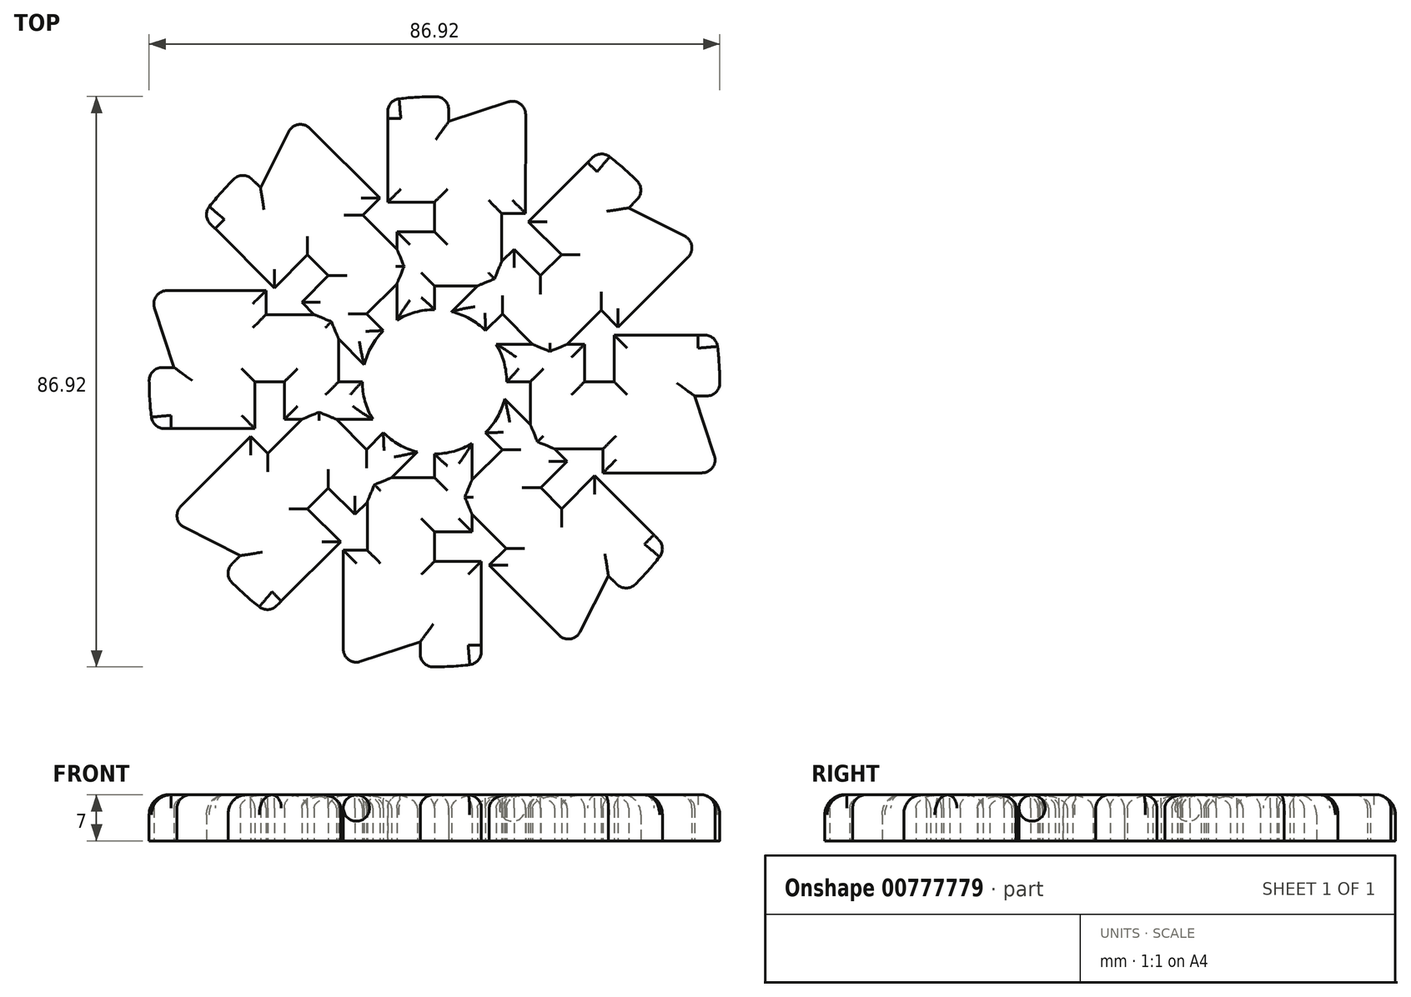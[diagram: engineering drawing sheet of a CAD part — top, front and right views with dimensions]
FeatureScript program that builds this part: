
annotation { "Feature Type Name" : "Feature", "Feature Type Description" : "" }
export const myFeature = defineFeature(function(context is Context, id is Id, definition is map)
    precondition{}
    {
        {
            var Q0;
            Q0=qCreatedBy(makeId("Top.planeOp"),FACE);
            var sketch = newSketch(context, id + "F0", { "sketchPlane" : qUnion([Q0])});
            skCircle(sketch, "E0", {"center": v(0, 0) * mm, "radius": 35 * mm});
            skCircle(sketch, "E1", {"center": v(0, 0) * mm, "radius": 11 * mm});
            skSolve(sketch);
        }
        {
            var Q0;
            Q0=qCreatedBy(makeId("Top.planeOp"),FACE);
            var sketch = newSketch(context, id + "F1", { "sketchPlane" : qUnion([Q0])});
            skLineSegment(sketch, "E2.top", {"start": v(0, 22.87) * mm, "end": v(-5.72, 22.87) * mm});
            skLineSegment(sketch, "E2.right", {"start": v(-5.72, 9.4) * mm, "end": v(-5.72, 22.87) * mm});
            skLineSegment(sketch, "E3.top", {"start": v(0, 14.6) * mm, "end": v(10.24, 14.6) * mm});
            skLineSegment(sketch, "E3.right", {"start": v(10.24, 25.67) * mm, "end": v(10.24, 14.6) * mm});
            skLineSegment(sketch, "E4.bottom", {"start": v(2.18, 39.65) * mm, "end": v(13.89, 43.5) * mm});
            skLineSegment(sketch, "E4.left", {"start": v(0, 27.37) * mm, "end": v(0, 22.87) * mm});
            skLineSegment(sketch, "E4.right", {"start": v(13.89, 43.5) * mm, "end": v(13.88, 25.67) * mm});
            skLineSegment(sketch, "E5.top", {"start": v(-7.13, 27.37) * mm, "end": v(0, 27.37) * mm});
            skPoint(sketch, "E6.orphan", {"position": v(0, 38.94) * mm});
            skLineSegment(sketch, "E7.trimOffspring", {"start": v(10.24, 25.67) * mm, "end": v(13.88, 25.67) * mm});
            skArc(sketch, "E8", {"start": v(0, 11) * mm, "mid": v(-2.97, 10.6) * mm, "end": v(-5.72, 9.4) * mm});
            skLineSegment(sketch, "E9", {"start": v(0, 14.6) * mm, "end": v(0, 11) * mm});
            skLineSegment(sketch, "E10", {"start": v(-7.13, 27.37) * mm, "end": v(-7.13, 42.87) * mm});
            skLineSegment(sketch, "E11", {"start": v(2.18, 39.65) * mm, "end": v(2.18, 43.41) * mm});
            skArc(sketch, "E12", {"start": v(2.18, 43.41) * mm, "mid": v(-2.5, 43.38) * mm, "end": v(-7.13, 42.87) * mm});
            skLineSegment(sketch, "E13.1.0", {"start": v(-16.17, 16.16) * mm, "end": v(-20.21, 12.13) * mm});
            skLineSegment(sketch, "E13.1.1", {"start": v(-10.33, 10.33) * mm, "end": v(-7.78, 7.78) * mm});
            skLineSegment(sketch, "E13.1.2", {"start": v(-20.94, 40.59) * mm, "end": v(-8.34, 27.97) * mm});
            skLineSegment(sketch, "E13.1.3", {"start": v(-10.33, 10.33) * mm, "end": v(-3.09, 17.57) * mm});
            skPoint(sketch, "E13.1.4", {"position": v(-27.53, 27.53) * mm});
            skLineSegment(sketch, "E13.1.5", {"start": v(-19.36, 19.35) * mm, "end": v(-16.17, 16.16) * mm});
            skLineSegment(sketch, "E13.1.6", {"start": v(-10.69, 2.6) * mm, "end": v(-20.21, 12.13) * mm});
            skLineSegment(sketch, "E13.1.7", {"start": v(-24.4, 14.3) * mm, "end": v(-35.36, 25.27) * mm});
            skLineSegment(sketch, "E13.1.8", {"start": v(-26.5, 29.58) * mm, "end": v(-20.94, 40.59) * mm});
            skLineSegment(sketch, "E13.1.9", {"start": v(-26.5, 29.58) * mm, "end": v(-22.7, 25.77) * mm});
            skArc(sketch, "E13.1.10", {"start": v(-29.16, 32.24) * mm, "mid": v(-32.44, 28.91) * mm, "end": v(-35.36, 25.27) * mm});
            skLineSegment(sketch, "E13.1.11", {"start": v(-10.91, 25.4) * mm, "end": v(-3.09, 17.57) * mm});
            skLineSegment(sketch, "E13.1.12", {"start": v(-24.4, 14.3) * mm, "end": v(-19.36, 19.35) * mm});
            skArc(sketch, "E13.1.13", {"start": v(-7.78, 7.78) * mm, "mid": v(-9.59, 5.39) * mm, "end": v(-10.69, 2.6) * mm});
            skLineSegment(sketch, "E13.1.14", {"start": v(-10.91, 25.4) * mm, "end": v(-8.34, 27.97) * mm});
            skLineSegment(sketch, "E13.1.15", {"start": v(-22.7, 25.77) * mm, "end": v(-29.16, 32.24) * mm});
            skLineSegment(sketch, "E13.2.0", {"start": v(-22.87, 0) * mm, "end": v(-22.87, -5.72) * mm});
            skLineSegment(sketch, "E13.2.1", {"start": v(-14.6, 0) * mm, "end": v(-11, 0) * mm});
            skLineSegment(sketch, "E13.2.2", {"start": v(-43.5, 13.89) * mm, "end": v(-25.67, 13.88) * mm});
            skLineSegment(sketch, "E13.2.3", {"start": v(-14.6, 0) * mm, "end": v(-14.6, 10.24) * mm});
            skPoint(sketch, "E13.2.4", {"position": v(-38.94, 0) * mm});
            skLineSegment(sketch, "E13.2.5", {"start": v(-27.37, 0) * mm, "end": v(-22.87, 0) * mm});
            skLineSegment(sketch, "E13.2.6", {"start": v(-9.4, -5.72) * mm, "end": v(-22.87, -5.72) * mm});
            skLineSegment(sketch, "E13.2.7", {"start": v(-27.37, -7.13) * mm, "end": v(-42.87, -7.13) * mm});
            skLineSegment(sketch, "E13.2.8", {"start": v(-39.65, 2.18) * mm, "end": v(-43.5, 13.89) * mm});
            skLineSegment(sketch, "E13.2.9", {"start": v(-39.65, 2.18) * mm, "end": v(-34.27, 2.18) * mm});
            skArc(sketch, "E13.2.10", {"start": v(-43.41, 2.18) * mm, "mid": v(-43.38, -2.5) * mm, "end": v(-42.87, -7.13) * mm});
            skLineSegment(sketch, "E13.2.11", {"start": v(-25.67, 10.24) * mm, "end": v(-14.6, 10.24) * mm});
            skLineSegment(sketch, "E13.2.12", {"start": v(-27.37, -7.13) * mm, "end": v(-27.37, 0) * mm});
            skArc(sketch, "E13.2.13", {"start": v(-11, 0) * mm, "mid": v(-10.6, -2.97) * mm, "end": v(-9.4, -5.72) * mm});
            skLineSegment(sketch, "E13.2.14", {"start": v(-25.67, 10.24) * mm, "end": v(-25.67, 13.88) * mm});
            skLineSegment(sketch, "E13.2.15", {"start": v(-34.27, 2.18) * mm, "end": v(-43.41, 2.18) * mm});
            skLineSegment(sketch, "E13.3.0", {"start": v(-16.16, -16.17) * mm, "end": v(-12.13, -20.21) * mm});
            skLineSegment(sketch, "E13.3.1", {"start": v(-10.33, -10.33) * mm, "end": v(-7.78, -7.78) * mm});
            skLineSegment(sketch, "E13.3.2", {"start": v(-40.59, -20.94) * mm, "end": v(-27.97, -8.34) * mm});
            skLineSegment(sketch, "E13.3.3", {"start": v(-10.33, -10.33) * mm, "end": v(-17.57, -3.09) * mm});
            skPoint(sketch, "E13.3.4", {"position": v(-27.53, -27.53) * mm});
            skLineSegment(sketch, "E13.3.5", {"start": v(-19.35, -19.36) * mm, "end": v(-16.16, -16.17) * mm});
            skLineSegment(sketch, "E13.3.6", {"start": v(-2.6, -10.69) * mm, "end": v(-12.13, -20.21) * mm});
            skLineSegment(sketch, "E13.3.7", {"start": v(-14.3, -24.4) * mm, "end": v(-25.27, -35.36) * mm});
            skLineSegment(sketch, "E13.3.8", {"start": v(-29.58, -26.5) * mm, "end": v(-40.59, -20.94) * mm});
            skLineSegment(sketch, "E13.3.9", {"start": v(-29.58, -26.5) * mm, "end": v(-25.77, -22.7) * mm});
            skArc(sketch, "E13.3.10", {"start": v(-32.24, -29.16) * mm, "mid": v(-28.91, -32.44) * mm, "end": v(-25.27, -35.36) * mm});
            skLineSegment(sketch, "E13.3.11", {"start": v(-25.4, -10.91) * mm, "end": v(-17.57, -3.09) * mm});
            skLineSegment(sketch, "E13.3.12", {"start": v(-14.3, -24.4) * mm, "end": v(-19.35, -19.36) * mm});
            skArc(sketch, "E13.3.13", {"start": v(-7.78, -7.78) * mm, "mid": v(-5.39, -9.59) * mm, "end": v(-2.6, -10.69) * mm});
            skLineSegment(sketch, "E13.3.14", {"start": v(-25.4, -10.91) * mm, "end": v(-27.97, -8.34) * mm});
            skLineSegment(sketch, "E13.3.15", {"start": v(-25.77, -22.7) * mm, "end": v(-32.24, -29.16) * mm});
            skLineSegment(sketch, "E13.4.0", {"start": v(0, -22.87) * mm, "end": v(5.72, -22.87) * mm});
            skLineSegment(sketch, "E13.4.1", {"start": v(0, -14.6) * mm, "end": v(0, -11) * mm});
            skLineSegment(sketch, "E13.4.2", {"start": v(-13.89, -43.5) * mm, "end": v(-13.88, -25.67) * mm});
            skLineSegment(sketch, "E13.4.3", {"start": v(0, -14.6) * mm, "end": v(-10.24, -14.6) * mm});
            skPoint(sketch, "E13.4.4", {"position": v(0, -38.94) * mm});
            skLineSegment(sketch, "E13.4.5", {"start": v(0, -27.37) * mm, "end": v(0, -22.87) * mm});
            skLineSegment(sketch, "E13.4.6", {"start": v(5.72, -9.4) * mm, "end": v(5.72, -22.87) * mm});
            skLineSegment(sketch, "E13.4.7", {"start": v(7.13, -27.37) * mm, "end": v(7.13, -42.87) * mm});
            skLineSegment(sketch, "E13.4.8", {"start": v(-2.18, -39.65) * mm, "end": v(-13.89, -43.5) * mm});
            skLineSegment(sketch, "E13.4.9", {"start": v(-2.18, -39.65) * mm, "end": v(-2.18, -34.27) * mm});
            skArc(sketch, "E13.4.10", {"start": v(-2.18, -43.41) * mm, "mid": v(2.5, -43.38) * mm, "end": v(7.13, -42.87) * mm});
            skLineSegment(sketch, "E13.4.11", {"start": v(-10.24, -25.67) * mm, "end": v(-10.24, -14.6) * mm});
            skLineSegment(sketch, "E13.4.12", {"start": v(7.13, -27.37) * mm, "end": v(0, -27.37) * mm});
            skArc(sketch, "E13.4.13", {"start": v(0, -11) * mm, "mid": v(2.97, -10.6) * mm, "end": v(5.72, -9.4) * mm});
            skLineSegment(sketch, "E13.4.14", {"start": v(-10.24, -25.67) * mm, "end": v(-13.88, -25.67) * mm});
            skLineSegment(sketch, "E13.4.15", {"start": v(-2.18, -34.27) * mm, "end": v(-2.18, -43.41) * mm});
            skLineSegment(sketch, "E13.5.0", {"start": v(16.17, -16.16) * mm, "end": v(20.21, -12.13) * mm});
            skLineSegment(sketch, "E13.5.1", {"start": v(10.33, -10.33) * mm, "end": v(7.78, -7.78) * mm});
            skLineSegment(sketch, "E13.5.2", {"start": v(20.94, -40.59) * mm, "end": v(8.34, -27.97) * mm});
            skLineSegment(sketch, "E13.5.3", {"start": v(10.33, -10.33) * mm, "end": v(3.09, -17.57) * mm});
            skPoint(sketch, "E13.5.4", {"position": v(27.53, -27.53) * mm});
            skLineSegment(sketch, "E13.5.5", {"start": v(19.36, -19.35) * mm, "end": v(16.17, -16.16) * mm});
            skLineSegment(sketch, "E13.5.6", {"start": v(10.69, -2.6) * mm, "end": v(20.21, -12.13) * mm});
            skLineSegment(sketch, "E13.5.7", {"start": v(24.4, -14.3) * mm, "end": v(35.36, -25.27) * mm});
            skLineSegment(sketch, "E13.5.8", {"start": v(26.5, -29.58) * mm, "end": v(20.94, -40.59) * mm});
            skLineSegment(sketch, "E13.5.9", {"start": v(26.5, -29.58) * mm, "end": v(22.7, -25.77) * mm});
            skArc(sketch, "E13.5.10", {"start": v(29.16, -32.24) * mm, "mid": v(32.44, -28.91) * mm, "end": v(35.36, -25.27) * mm});
            skLineSegment(sketch, "E13.5.11", {"start": v(10.91, -25.4) * mm, "end": v(3.09, -17.57) * mm});
            skLineSegment(sketch, "E13.5.12", {"start": v(24.4, -14.3) * mm, "end": v(19.36, -19.35) * mm});
            skArc(sketch, "E13.5.13", {"start": v(7.78, -7.78) * mm, "mid": v(9.59, -5.39) * mm, "end": v(10.69, -2.6) * mm});
            skLineSegment(sketch, "E13.5.14", {"start": v(10.91, -25.4) * mm, "end": v(8.34, -27.97) * mm});
            skLineSegment(sketch, "E13.5.15", {"start": v(22.7, -25.77) * mm, "end": v(29.16, -32.24) * mm});
            skLineSegment(sketch, "E13.6.0", {"start": v(22.87, 0) * mm, "end": v(22.87, 5.72) * mm});
            skLineSegment(sketch, "E13.6.1", {"start": v(14.6, 0) * mm, "end": v(11, 0) * mm});
            skLineSegment(sketch, "E13.6.2", {"start": v(43.5, -13.89) * mm, "end": v(25.67, -13.88) * mm});
            skLineSegment(sketch, "E13.6.3", {"start": v(14.6, 0) * mm, "end": v(14.6, -10.24) * mm});
            skPoint(sketch, "E13.6.4", {"position": v(38.94, 0) * mm});
            skLineSegment(sketch, "E13.6.5", {"start": v(27.37, 0) * mm, "end": v(22.87, 0) * mm});
            skLineSegment(sketch, "E13.6.6", {"start": v(9.4, 5.72) * mm, "end": v(22.87, 5.72) * mm});
            skLineSegment(sketch, "E13.6.7", {"start": v(27.37, 7.13) * mm, "end": v(42.87, 7.13) * mm});
            skLineSegment(sketch, "E13.6.8", {"start": v(39.65, -2.18) * mm, "end": v(43.5, -13.89) * mm});
            skLineSegment(sketch, "E13.6.9", {"start": v(39.65, -2.18) * mm, "end": v(34.27, -2.18) * mm});
            skArc(sketch, "E13.6.10", {"start": v(43.41, -2.18) * mm, "mid": v(43.38, 2.5) * mm, "end": v(42.87, 7.13) * mm});
            skLineSegment(sketch, "E13.6.11", {"start": v(25.67, -10.24) * mm, "end": v(14.6, -10.24) * mm});
            skLineSegment(sketch, "E13.6.12", {"start": v(27.37, 7.13) * mm, "end": v(27.37, 0) * mm});
            skArc(sketch, "E13.6.13", {"start": v(11, 0) * mm, "mid": v(10.6, 2.97) * mm, "end": v(9.4, 5.72) * mm});
            skLineSegment(sketch, "E13.6.14", {"start": v(25.67, -10.24) * mm, "end": v(25.67, -13.88) * mm});
            skLineSegment(sketch, "E13.6.15", {"start": v(34.27, -2.18) * mm, "end": v(43.41, -2.18) * mm});
            skLineSegment(sketch, "E13.7.0", {"start": v(16.16, 16.17) * mm, "end": v(12.13, 20.21) * mm});
            skLineSegment(sketch, "E13.7.1", {"start": v(10.33, 10.33) * mm, "end": v(7.78, 7.78) * mm});
            skLineSegment(sketch, "E13.7.2", {"start": v(40.59, 20.94) * mm, "end": v(27.97, 8.34) * mm});
            skLineSegment(sketch, "E13.7.3", {"start": v(10.33, 10.33) * mm, "end": v(17.57, 3.09) * mm});
            skPoint(sketch, "E13.7.4", {"position": v(27.53, 27.53) * mm});
            skLineSegment(sketch, "E13.7.5", {"start": v(19.35, 19.36) * mm, "end": v(16.16, 16.17) * mm});
            skLineSegment(sketch, "E13.7.6", {"start": v(2.6, 10.69) * mm, "end": v(12.13, 20.21) * mm});
            skLineSegment(sketch, "E13.7.7", {"start": v(14.3, 24.4) * mm, "end": v(25.27, 35.36) * mm});
            skLineSegment(sketch, "E13.7.8", {"start": v(29.58, 26.5) * mm, "end": v(40.59, 20.94) * mm});
            skLineSegment(sketch, "E13.7.9", {"start": v(29.58, 26.5) * mm, "end": v(25.77, 22.7) * mm});
            skArc(sketch, "E13.7.10", {"start": v(32.24, 29.16) * mm, "mid": v(28.91, 32.44) * mm, "end": v(25.27, 35.36) * mm});
            skLineSegment(sketch, "E13.7.11", {"start": v(25.4, 10.91) * mm, "end": v(17.57, 3.09) * mm});
            skLineSegment(sketch, "E13.7.12", {"start": v(14.3, 24.4) * mm, "end": v(19.35, 19.36) * mm});
            skArc(sketch, "E13.7.13", {"start": v(7.78, 7.78) * mm, "mid": v(5.39, 9.59) * mm, "end": v(2.6, 10.69) * mm});
            skLineSegment(sketch, "E13.7.14", {"start": v(25.4, 10.91) * mm, "end": v(27.97, 8.34) * mm});
            skLineSegment(sketch, "E13.7.15", {"start": v(25.77, 22.7) * mm, "end": v(32.24, 29.16) * mm});
            skPoint(sketch, "E14.orphan", {"position": v(2.18, 34.27) * mm});
            skSolve(sketch);
        }
        {
            var Q0;
            Q0=qSketchRegion(id+"F1",true);
            extrude(context, id + "F2", {"entities" : qUnion([Q0]), "depth" : 7 * mm, "offsetDistance" : 25 * mm});
        }
        {
            var Q0;
            Q0=makeQuery(id+"F2.opExtrude","CAP_EDGE",EDGE,{"disambiguationData":[OSD([sQuery(id+"F1.wireOp",EDGE,"E13.5.10")])],"isStart":false});
            var Q1;
            Q1=makeQuery(id+"F2.opExtrude","CAP_EDGE",EDGE,{"disambiguationData":[OSD([sQuery(id+"F1.wireOp",EDGE,"E13.4.10")])],"isStart":false});
            var Q2;
            Q2=makeQuery(id+"F2.opExtrude","CAP_EDGE",EDGE,{"disambiguationData":[OSD([sQuery(id+"F1.wireOp",EDGE,"E13.6.10")])],"isStart":false});
            var Q3;
            Q3=makeQuery(id+"F2.opExtrude","CAP_EDGE",EDGE,{"disambiguationData":[OSD([sQuery(id+"F1.wireOp",EDGE,"E13.7.10")])],"isStart":false});
            var Q4;
            Q4=makeQuery(id+"F2.opExtrude","CAP_EDGE",EDGE,{"disambiguationData":[OSD([sQuery(id+"F1.wireOp",EDGE,"E12")])],"isStart":false});
            var Q5;
            Q5=makeQuery(id+"F2.opExtrude","CAP_EDGE",EDGE,{"disambiguationData":[OSD([sQuery(id+"F1.wireOp",EDGE,"E13.1.10")])],"isStart":false});
            var Q6;
            Q6=makeQuery(id+"F2.opExtrude","CAP_EDGE",EDGE,{"disambiguationData":[OSD([sQuery(id+"F1.wireOp",EDGE,"E13.2.10")])],"isStart":false});
            fillet(context, id + "F3", {"entities" : qUnion([Q0, Q1, Q2, Q3, Q4, Q5, Q6]), "radius" : 3 * mm, "tangentPropagation" : true, "allowEdgeOverflow" : false});
        }
        {
            var Q0;
            Q0=makeQuery(id+"F2.opExtrude","CAP_EDGE",EDGE,{"disambiguationData":[OSD([sQuery(id+"F1.wireOp",EDGE,"E13.3.10")])],"isStart":false});
            fillet(context, id + "F4", {"entities" : qUnion([Q0]), "radius" : 3 * mm, "tangentPropagation" : true, "allowEdgeOverflow" : false});
        }
        {
            var Q0;
            Q0=makeQuery(id+"F2.opExtrude","SWEPT_EDGE",EDGE,{"disambiguationData":[OSD([sQuery(id+"F1.wireOp",EDGE,"E13.1.2"),sQuery(id+"F1.wireOp",EDGE,"E13.1.8")])]});
            var Q1;
            Q1=makeQuery(id+"F2.opExtrude","SWEPT_EDGE",EDGE,{"disambiguationData":[OSD([sQuery(id+"F1.wireOp",EDGE,"E4.bottom"),sQuery(id+"F1.wireOp",EDGE,"E4.right")])]});
            var Q2;
            Q2=makeQuery(id+"F2.opExtrude","SWEPT_EDGE",EDGE,{"disambiguationData":[OSD([sQuery(id+"F1.wireOp",EDGE,"E13.7.2"),sQuery(id+"F1.wireOp",EDGE,"E13.7.8")])]});
            var Q3;
            Q3=makeQuery(id+"F2.opExtrude","SWEPT_EDGE",EDGE,{"disambiguationData":[OSD([sQuery(id+"F1.wireOp",EDGE,"E13.6.2"),sQuery(id+"F1.wireOp",EDGE,"E13.6.8")])]});
            var Q4;
            Q4=makeQuery(id+"F2.opExtrude","SWEPT_EDGE",EDGE,{"disambiguationData":[OSD([sQuery(id+"F1.wireOp",EDGE,"E13.5.2"),sQuery(id+"F1.wireOp",EDGE,"E13.5.8")])]});
            var Q5;
            Q5=makeQuery(id+"F2.opExtrude","SWEPT_EDGE",EDGE,{"disambiguationData":[OSD([sQuery(id+"F1.wireOp",EDGE,"E13.4.2"),sQuery(id+"F1.wireOp",EDGE,"E13.4.8")])]});
            var Q6;
            Q6=makeQuery(id+"F2.opExtrude","SWEPT_EDGE",EDGE,{"disambiguationData":[OSD([sQuery(id+"F1.wireOp",EDGE,"E13.3.2"),sQuery(id+"F1.wireOp",EDGE,"E13.3.8")])]});
            var Q7;
            Q7=makeQuery(id+"F2.opExtrude","SWEPT_EDGE",EDGE,{"disambiguationData":[OSD([sQuery(id+"F1.wireOp",EDGE,"E13.2.2"),sQuery(id+"F1.wireOp",EDGE,"E13.2.8")])]});
            fillet(context, id + "F5", {"entities" : qUnion([Q0, Q1, Q2, Q3, Q4, Q5, Q6, Q7]), "radius" : 2 * mm, "tangentPropagation" : true, "allowEdgeOverflow" : false});
        }
        {
            var Q0;
            {var subQ0=sQuery(id+"F1.wireOp",EDGE,"E13.6.6");Q0=makeQuery(id+"F2.opExtrude","CAP_EDGE",EDGE,{"disambiguationData":[OSD([subQ0]),TDD([makeQuery(id+"F1.imprint","IMPRINT",EDGE,{"disambiguationData":[TD([[makeQuery(id+"F1.imprint","INTERSECT",VERTEX,{"derivedFrom":[sQuery(id+"F1.wireOp",EDGE,"E13.6.0"),subQ0]}),1.0]])],"derivedFrom":subQ0})])],"isStart":false});}
            var Q1;
            Q1=makeQuery(id+"F2.opExtrude","CAP_EDGE",EDGE,{"disambiguationData":[OSD([sQuery(id+"F1.wireOp",EDGE,"E13.7.11")])],"isStart":false});
            var Q2;
            Q2=makeQuery(id+"F2.opExtrude","CAP_EDGE",EDGE,{"disambiguationData":[OSD([sQuery(id+"F1.wireOp",EDGE,"E3.right")])],"isStart":false});
            var Q3;
            {var subQ0=sQuery(id+"F1.wireOp",EDGE,"E13.7.6");Q3=makeQuery(id+"F2.opExtrude","CAP_EDGE",EDGE,{"disambiguationData":[OSD([subQ0]),TDD([makeQuery(id+"F1.imprint","IMPRINT",EDGE,{"disambiguationData":[TD([[makeQuery(id+"F1.imprint","INTERSECT",VERTEX,{"derivedFrom":[sQuery(id+"F1.wireOp",EDGE,"E13.7.0"),subQ0]}),1.0]])],"derivedFrom":subQ0})])],"isStart":false});}
            var Q4;
            Q4=makeQuery(id+"F2.opExtrude","CAP_EDGE",EDGE,{"disambiguationData":[OSD([sQuery(id+"F1.wireOp",EDGE,"E13.1.11")])],"isStart":false});
            var Q5;
            {var subQ0=sQuery(id+"F1.wireOp",EDGE,"E2.right");Q5=makeQuery(id+"F2.opExtrude","CAP_EDGE",EDGE,{"disambiguationData":[OSD([subQ0]),TDD([makeQuery(id+"F1.imprint","IMPRINT",EDGE,{"disambiguationData":[TD([[makeQuery(id+"F1.imprint","INTERSECT",VERTEX,{"derivedFrom":[sQuery(id+"F1.wireOp",EDGE,"E2.top"),subQ0]}),1.0]])],"derivedFrom":subQ0})])],"isStart":false});}
            var Q6;
            Q6=makeQuery(id+"F2.opExtrude","CAP_EDGE",EDGE,{"disambiguationData":[OSD([sQuery(id+"F1.wireOp",EDGE,"E13.2.11")])],"isStart":false});
            var Q7;
            {var subQ0=sQuery(id+"F1.wireOp",EDGE,"E13.1.6");Q7=makeQuery(id+"F2.opExtrude","CAP_EDGE",EDGE,{"disambiguationData":[OSD([subQ0]),TDD([makeQuery(id+"F1.imprint","IMPRINT",EDGE,{"disambiguationData":[TD([[makeQuery(id+"F1.imprint","INTERSECT",VERTEX,{"derivedFrom":[sQuery(id+"F1.wireOp",EDGE,"E13.1.0"),subQ0]}),1.0]])],"derivedFrom":subQ0})])],"isStart":false});}
            var Q8;
            Q8=makeQuery(id+"F2.opExtrude","CAP_EDGE",EDGE,{"disambiguationData":[OSD([sQuery(id+"F1.wireOp",EDGE,"E13.3.11")])],"isStart":false});
            var Q9;
            {var subQ0=sQuery(id+"F1.wireOp",EDGE,"E13.2.6");Q9=makeQuery(id+"F2.opExtrude","CAP_EDGE",EDGE,{"disambiguationData":[OSD([subQ0]),TDD([makeQuery(id+"F1.imprint","IMPRINT",EDGE,{"disambiguationData":[TD([[makeQuery(id+"F1.imprint","INTERSECT",VERTEX,{"derivedFrom":[sQuery(id+"F1.wireOp",EDGE,"E13.2.0"),subQ0]}),1.0]])],"derivedFrom":subQ0})])],"isStart":false});}
            var Q10;
            {var subQ0=sQuery(id+"F1.wireOp",EDGE,"E13.3.6");Q10=makeQuery(id+"F2.opExtrude","CAP_EDGE",EDGE,{"disambiguationData":[OSD([subQ0]),TDD([makeQuery(id+"F1.imprint","IMPRINT",EDGE,{"disambiguationData":[TD([[makeQuery(id+"F1.imprint","INTERSECT",VERTEX,{"derivedFrom":[sQuery(id+"F1.wireOp",EDGE,"E13.3.0"),subQ0]}),1.0]])],"derivedFrom":subQ0})])],"isStart":false});}
            var Q11;
            Q11=makeQuery(id+"F2.opExtrude","CAP_EDGE",EDGE,{"disambiguationData":[OSD([sQuery(id+"F1.wireOp",EDGE,"E13.4.11")])],"isStart":false});
            var Q12;
            {var subQ0=sQuery(id+"F1.wireOp",EDGE,"E13.4.6");Q12=makeQuery(id+"F2.opExtrude","CAP_EDGE",EDGE,{"disambiguationData":[OSD([subQ0]),TDD([makeQuery(id+"F1.imprint","IMPRINT",EDGE,{"disambiguationData":[TD([[makeQuery(id+"F1.imprint","INTERSECT",VERTEX,{"derivedFrom":[sQuery(id+"F1.wireOp",EDGE,"E13.4.0"),subQ0]}),1.0]])],"derivedFrom":subQ0})])],"isStart":false});}
            var Q13;
            Q13=makeQuery(id+"F2.opExtrude","CAP_EDGE",EDGE,{"disambiguationData":[OSD([sQuery(id+"F1.wireOp",EDGE,"E13.5.11")])],"isStart":false});
            var Q14;
            Q14=makeQuery(id+"F2.opExtrude","CAP_EDGE",EDGE,{"disambiguationData":[OSD([sQuery(id+"F1.wireOp",EDGE,"E13.6.11")])],"isStart":false});
            var Q15;
            {var subQ0=sQuery(id+"F1.wireOp",EDGE,"E13.5.6");Q15=makeQuery(id+"F2.opExtrude","CAP_EDGE",EDGE,{"disambiguationData":[OSD([subQ0]),TDD([makeQuery(id+"F1.imprint","IMPRINT",EDGE,{"disambiguationData":[TD([[makeQuery(id+"F1.imprint","INTERSECT",VERTEX,{"derivedFrom":[sQuery(id+"F1.wireOp",EDGE,"E13.5.0"),subQ0]}),1.0]])],"derivedFrom":subQ0})])],"isStart":false});}
            var Q16;
            Q16=makeQuery(id+"F2.opExtrude","CAP_FACE",FACE,{"disambiguationData":[OSD([sQuery(id+"F1.wireOp",EDGE,"E2.top"),sQuery(id+"F1.wireOp",EDGE,"E2.right"),sQuery(id+"F1.wireOp",EDGE,"E3.top"),sQuery(id+"F1.wireOp",EDGE,"E3.right"),sQuery(id+"F1.wireOp",EDGE,"E4.bottom"),sQuery(id+"F1.wireOp",EDGE,"E4.left"),sQuery(id+"F1.wireOp",EDGE,"E4.right"),sQuery(id+"F1.wireOp",EDGE,"E5.top"),sQuery(id+"F1.wireOp",EDGE,"E7.trimOffspring"),sQuery(id+"F1.wireOp",EDGE,"E8"),sQuery(id+"F1.wireOp",EDGE,"E9"),sQuery(id+"F1.wireOp",EDGE,"E10"),sQuery(id+"F1.wireOp",EDGE,"E11"),sQuery(id+"F1.wireOp",EDGE,"E12"),sQuery(id+"F1.wireOp",EDGE,"E13.1.0"),sQuery(id+"F1.wireOp",EDGE,"E13.1.1"),sQuery(id+"F1.wireOp",EDGE,"E13.1.2"),sQuery(id+"F1.wireOp",EDGE,"E13.1.3"),sQuery(id+"F1.wireOp",EDGE,"E13.1.5"),sQuery(id+"F1.wireOp",EDGE,"E13.1.6"),sQuery(id+"F1.wireOp",EDGE,"E13.1.7"),sQuery(id+"F1.wireOp",EDGE,"E13.1.8"),sQuery(id+"F1.wireOp",EDGE,"E13.1.10"),sQuery(id+"F1.wireOp",EDGE,"E13.1.11"),sQuery(id+"F1.wireOp",EDGE,"E13.1.12"),sQuery(id+"F1.wireOp",EDGE,"E13.1.13"),sQuery(id+"F1.wireOp",EDGE,"E13.1.14"),sQuery(id+"F1.wireOp",EDGE,"E13.1.15"),sQuery(id+"F1.wireOp",EDGE,"E13.2.0"),sQuery(id+"F1.wireOp",EDGE,"E13.2.1"),sQuery(id+"F1.wireOp",EDGE,"E13.2.2"),sQuery(id+"F1.wireOp",EDGE,"E13.2.3"),sQuery(id+"F1.wireOp",EDGE,"E13.2.5"),sQuery(id+"F1.wireOp",EDGE,"E13.2.6"),sQuery(id+"F1.wireOp",EDGE,"E13.2.7"),sQuery(id+"F1.wireOp",EDGE,"E13.2.8"),sQuery(id+"F1.wireOp",EDGE,"E13.2.10"),sQuery(id+"F1.wireOp",EDGE,"E13.2.11"),sQuery(id+"F1.wireOp",EDGE,"E13.2.12"),sQuery(id+"F1.wireOp",EDGE,"E13.2.13"),sQuery(id+"F1.wireOp",EDGE,"E13.2.14"),sQuery(id+"F1.wireOp",EDGE,"E13.2.15"),sQuery(id+"F1.wireOp",EDGE,"E13.3.0"),sQuery(id+"F1.wireOp",EDGE,"E13.3.1"),sQuery(id+"F1.wireOp",EDGE,"E13.3.2"),sQuery(id+"F1.wireOp",EDGE,"E13.3.3"),sQuery(id+"F1.wireOp",EDGE,"E13.3.5"),sQuery(id+"F1.wireOp",EDGE,"E13.3.6"),sQuery(id+"F1.wireOp",EDGE,"E13.3.7"),sQuery(id+"F1.wireOp",EDGE,"E13.3.8"),sQuery(id+"F1.wireOp",EDGE,"E13.3.10"),sQuery(id+"F1.wireOp",EDGE,"E13.3.11"),sQuery(id+"F1.wireOp",EDGE,"E13.3.12"),sQuery(id+"F1.wireOp",EDGE,"E13.3.13"),sQuery(id+"F1.wireOp",EDGE,"E13.3.14"),sQuery(id+"F1.wireOp",EDGE,"E13.3.15"),sQuery(id+"F1.wireOp",EDGE,"E13.4.0"),sQuery(id+"F1.wireOp",EDGE,"E13.4.1"),sQuery(id+"F1.wireOp",EDGE,"E13.4.2"),sQuery(id+"F1.wireOp",EDGE,"E13.4.3"),sQuery(id+"F1.wireOp",EDGE,"E13.4.5"),sQuery(id+"F1.wireOp",EDGE,"E13.4.6"),sQuery(id+"F1.wireOp",EDGE,"E13.4.7"),sQuery(id+"F1.wireOp",EDGE,"E13.4.8"),sQuery(id+"F1.wireOp",EDGE,"E13.4.10"),sQuery(id+"F1.wireOp",EDGE,"E13.4.11"),sQuery(id+"F1.wireOp",EDGE,"E13.4.12"),sQuery(id+"F1.wireOp",EDGE,"E13.4.13"),sQuery(id+"F1.wireOp",EDGE,"E13.4.14"),sQuery(id+"F1.wireOp",EDGE,"E13.4.15"),sQuery(id+"F1.wireOp",EDGE,"E13.5.0"),sQuery(id+"F1.wireOp",EDGE,"E13.5.1"),sQuery(id+"F1.wireOp",EDGE,"E13.5.2"),sQuery(id+"F1.wireOp",EDGE,"E13.5.3"),sQuery(id+"F1.wireOp",EDGE,"E13.5.5"),sQuery(id+"F1.wireOp",EDGE,"E13.5.6"),sQuery(id+"F1.wireOp",EDGE,"E13.5.7"),sQuery(id+"F1.wireOp",EDGE,"E13.5.8"),sQuery(id+"F1.wireOp",EDGE,"E13.5.10"),sQuery(id+"F1.wireOp",EDGE,"E13.5.11"),sQuery(id+"F1.wireOp",EDGE,"E13.5.12"),sQuery(id+"F1.wireOp",EDGE,"E13.5.13"),sQuery(id+"F1.wireOp",EDGE,"E13.5.14"),sQuery(id+"F1.wireOp",EDGE,"E13.5.15"),sQuery(id+"F1.wireOp",EDGE,"E13.6.0"),sQuery(id+"F1.wireOp",EDGE,"E13.6.1"),sQuery(id+"F1.wireOp",EDGE,"E13.6.2"),sQuery(id+"F1.wireOp",EDGE,"E13.6.3"),sQuery(id+"F1.wireOp",EDGE,"E13.6.5"),sQuery(id+"F1.wireOp",EDGE,"E13.6.6"),sQuery(id+"F1.wireOp",EDGE,"E13.6.7"),sQuery(id+"F1.wireOp",EDGE,"E13.6.8"),sQuery(id+"F1.wireOp",EDGE,"E13.6.10"),sQuery(id+"F1.wireOp",EDGE,"E13.6.11"),sQuery(id+"F1.wireOp",EDGE,"E13.6.12"),sQuery(id+"F1.wireOp",EDGE,"E13.6.13"),sQuery(id+"F1.wireOp",EDGE,"E13.6.14"),sQuery(id+"F1.wireOp",EDGE,"E13.6.15"),sQuery(id+"F1.wireOp",EDGE,"E13.7.0"),sQuery(id+"F1.wireOp",EDGE,"E13.7.1"),sQuery(id+"F1.wireOp",EDGE,"E13.7.2"),sQuery(id+"F1.wireOp",EDGE,"E13.7.3"),sQuery(id+"F1.wireOp",EDGE,"E13.7.5"),sQuery(id+"F1.wireOp",EDGE,"E13.7.6"),sQuery(id+"F1.wireOp",EDGE,"E13.7.7"),sQuery(id+"F1.wireOp",EDGE,"E13.7.8"),sQuery(id+"F1.wireOp",EDGE,"E13.7.10"),sQuery(id+"F1.wireOp",EDGE,"E13.7.11"),sQuery(id+"F1.wireOp",EDGE,"E13.7.12"),sQuery(id+"F1.wireOp",EDGE,"E13.7.13"),sQuery(id+"F1.wireOp",EDGE,"E13.7.14"),sQuery(id+"F1.wireOp",EDGE,"E13.7.15")])],"isStart":false});
            fillet(context, id + "F6", {"entities" : qUnion([Q0, Q1, Q2, Q3, Q4, Q5, Q6, Q7, Q8, Q9, Q10, Q11, Q12, Q13, Q14, Q15, Q16]), "radius" : 2 * mm, "tangentPropagation" : true, "allowEdgeOverflow" : false});
        }
    });
